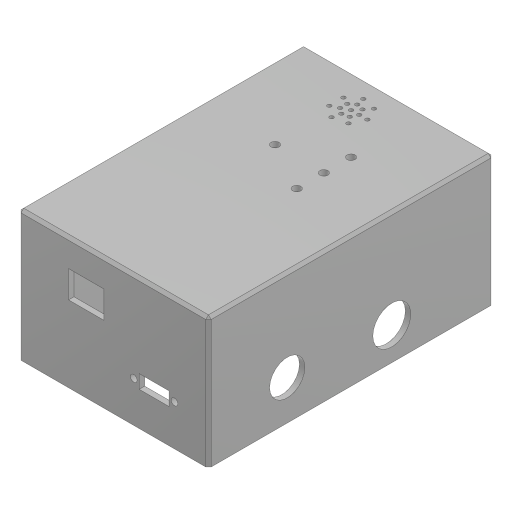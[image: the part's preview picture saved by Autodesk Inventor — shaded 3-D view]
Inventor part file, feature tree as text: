
AUTODESK INVENTOR PART (.ipt)
format: ipt  version: 2023.1 (Build 271208000, 208)  size: 330,752 bytes
history: native  units: mm
features: sketch x14, hole x8, extrude x7, chamfer x5, projected_geometry x2, shell x1, pattern_circular x1
ambient origin geometry x8: Origin, YZ Plane, XZ Plane, XY Plane, X Axis, Y Axis, Z Axis, Center Point
bodies: Volumenkörper1 (feature_tree)
feature tree (38):
  extrude  "Extrusion1"  Depth=70.0mm
  shell  "Wandung1"  Thickness=48.0mm
  extrude  "Extrusion12"  Depth=11.0mm
  chamfer  "Fase2"  Distance=3.0mm
  chamfer  "Fase3"  Distance=8.0mm
  chamfer  "Fase4"  Distance=5.0mm Angle=45.0deg
  chamfer  "Fase5"  Distance=5.0mm Angle=45.0deg
  hole  "Bohrung14"  [1 undecoded]
  chamfer  "Fase6"  Distance=2.0mm Angle=45.0deg
  hole  "Button"  [1 undecoded]
  hole  "LEDS"  [1 undecoded]
  hole  "Sensor"  [1 undecoded]
  extrude  "Extrusion14"  Depth=10.0mm
  sketch  "Skizze20"  dims[d112=8.0mm d113=6.0mm d114=4.0mm d115=2.0mm d116=90.0deg d117=8.0mm d118=20.594885mm d149=11.0mm]
  extrude  "Extrusion9"  Depth=15.0mm
  hole  "Switch"  [1 undecoded]
  hole  "nRF-Antenna"  [1 undecoded]
  extrude  "PCB-holder"  Depth=7.0mm
  hole  "LED Green"  [1 undecoded]
  extrude  "Arduino Programming"  Depth=12.5mm
  extrude  "USB-C"  Depth=12.5mm
  hole  "Bohrung16"  [1 undecoded]
  pattern_circular  "Runde Anordnung3"  [2 undecoded]
  sketch  "Skizze1"  dims[d0=105.0mm d1=70.0mm d2=48.0mm d3=0.0mm]
  sketch  "Skizze11"  dims[d4=2.0mm]
  sketch  "Skizze12"  dims[d84=14.0mm d85=6.0mm d86=4.0mm d87=2.0mm d88=90.0deg d89=5.0mm d90=20.594885mm]
  sketch  "Skizze14"  dims[d95=3.0mm d96=6.0mm d97=4.0mm d98=2.0mm d99=90.0deg d100=8.0mm d101=20.594885mm]
  sketch  "Skizze22"  dims[d150=5.0mm]
  sketch  "Skizze25"  dims[d153=15.0mm d154=3.0mm d155=0.0mm]
  projected_geometry  "Projizierte Kontur5"
  sketch  "Skizze26"  dims[d156=2.5mm d157=6.0mm d158=4.0mm d159=2.0mm d160=90.0deg d161=8.0mm d162=20.594885mm]
  sketch  "Skizze27"  dims[d192=13.0mm d193=6.0mm d194=4.0mm d195=2.0mm d196=90.0deg d197=8.0mm d198=20.594885mm]
  sketch  "Skizze28"  dims[d208=5.0mm]
  sketch  "Skizze29"  dims[d209=5.0mm d210=8.0mm d211=0.0mm d212=5.0mm d213=2.0mm d214=45.0deg d215=5.0mm d216=2.0mm d217=45.0deg]
  sketch  "Skizze30"  dims[d218=5.0mm d219=2.0mm d220=45.0deg d221=5.0mm d222=2.0mm d223=45.0deg]
  projected_geometry  "Projizierte Kontur6"
  sketch  "Skizze31"  dims[d224=97.0mm]
  sketch  "Skizze32"  dims[d225=62.0mm d226=2.8mm d227=6.0mm d228=4.0mm d229=2.0mm d230=90.0deg d231=8.0mm d232=0.0mm d233=1.0mm d234=2.0mm d235=45.0deg d238=18.0mm d239=5.0mm d240=10.0mm d241=10.0mm d249=15.0mm d250=23.5mm d251=14.5mm d252=7.0mm d253=87.0mm d254=52.0mm d255=2.8mm d256=10.0mm d257=0.0mm d258=10.0mm d259=15.0mm d260=29.0mm d261=15.0mm d262=0.5mm d263=0.0mm d268=10.0mm d269=8.0mm d271=3.0mm d272=6.0mm d273=4.0mm d274=2.0mm d275=90.0deg d276=8.0mm d277=20.594885mm d278=15.0mm d279=15.0mm d280=11.0mm d282=10.0mm d283=10.0mm d284=0.0mm d285=15.0mm d286=12.0mm d287=20.0mm d288=20.0mm d289=10.0mm d290=33.0mm d291=13.0mm d292=10.0mm d293=10.0mm d294=0.0mm d295=3.0mm d296=3.0mm d297=40.0mm d298=5.0mm d299=1.5mm d300=6.0mm d301=4.0mm d302=2.0mm d303=90.0deg d304=8.0mm d305=20.594885mm d306=70.0mm d307=360.0deg d309=12.5mm]
note: 10 required parameter values undecoded (feature->parameter linkage not recoverable at this tier; creation-order binding heuristic only, values carry confidence <= 0.55)
